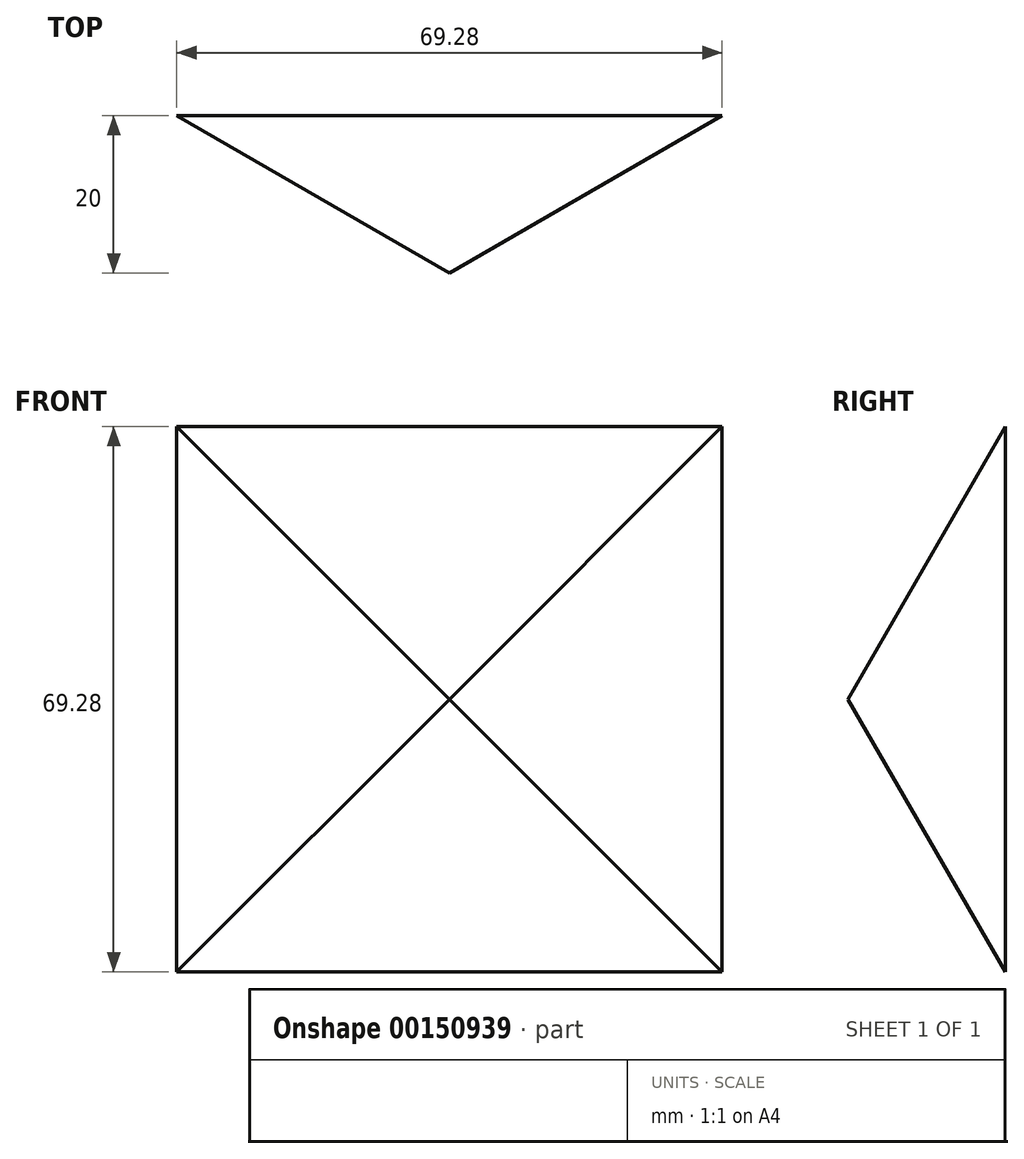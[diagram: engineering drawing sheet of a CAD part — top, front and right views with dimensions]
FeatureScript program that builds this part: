
annotation { "Feature Type Name" : "Feature", "Feature Type Description" : "" }
export const myFeature = defineFeature(function(context is Context, id is Id, definition is map)
    precondition{}
    {
        {
            var Q0;
            Q0=qCreatedBy(makeId("Top.planeOp"),FACE);
            var sketch = newSketch(context, id + "F0", { "sketchPlane" : qUnion([Q0])});
            skLineSegment(sketch, "E0", {"start": v(0, 0) * mm, "end": v(34.64, 20) * mm});
            skLineSegment(sketch, "E1", {"start": v(34.64, 20) * mm, "end": v(-34.64, 20) * mm});
            skLineSegment(sketch, "E2", {"start": v(-34.64, 20) * mm, "end": v(0, 0) * mm});
            skSolve(sketch);
        }
        {
            var Q0;
            Q0=makeQuery(id+"F0.imprint","IMPRINT",FACE,{"disambiguationData":[TD([[makeQuery(id+"F0.imprint","IMPRINT",EDGE,{"derivedFrom":sQuery(id+"F0.wireOp",EDGE,"E0")}),1.0]])]});
            extrude(context, id + "F1", {"entities" : qUnion([Q0]), "endBound" : BoundingType.SYMMETRIC, "depth" : 100 * mm});
        }
        {
            var Q0;
            Q0=qCreatedBy(makeId("Right.planeOp"),FACE);
            var sketch = newSketch(context, id + "F2", { "sketchPlane" : qUnion([Q0])});
            skLineSegment(sketch, "E3", {"start": v(0, 0) * mm, "end": v(20, -34.64) * mm});
            skLineSegment(sketch, "E4", {"start": v(20, -34.64) * mm, "end": v(20, 34.64) * mm});
            skLineSegment(sketch, "E5", {"start": v(20, 34.64) * mm, "end": v(0, 0) * mm});
            skPoint(sketch, "E6", {"position": v(0, 0) * mm});
            skLineSegment(sketch, "E7.bottom", {"start": v(50, 50) * mm, "end": v(-50, 50) * mm});
            skLineSegment(sketch, "E7.top", {"start": v(50, -50) * mm, "end": v(-50, -50) * mm});
            skLineSegment(sketch, "E7.left", {"start": v(50, 50) * mm, "end": v(50, -50) * mm});
            skLineSegment(sketch, "E7.right", {"start": v(-50, 50) * mm, "end": v(-50, -50) * mm});
            skSolve(sketch);
        }
        {
            var Q0;
            Q0=makeQuery(id+"F2.imprint","IMPRINT",FACE,{"disambiguationData":[TD([[makeQuery(id+"F2.imprint","IMPRINT",EDGE,{"derivedFrom":sQuery(id+"F2.wireOp",EDGE,"E3")}),-1.0]])]});
            extrude(context, id + "F3", {"entities" : qUnion([Q0]), "operationType" : NewBodyOperationType.REMOVE, "endBound" : BoundingType.SYMMETRIC, "oppositeDirection" : true, "depth" : 100 * mm});
        }
    });
